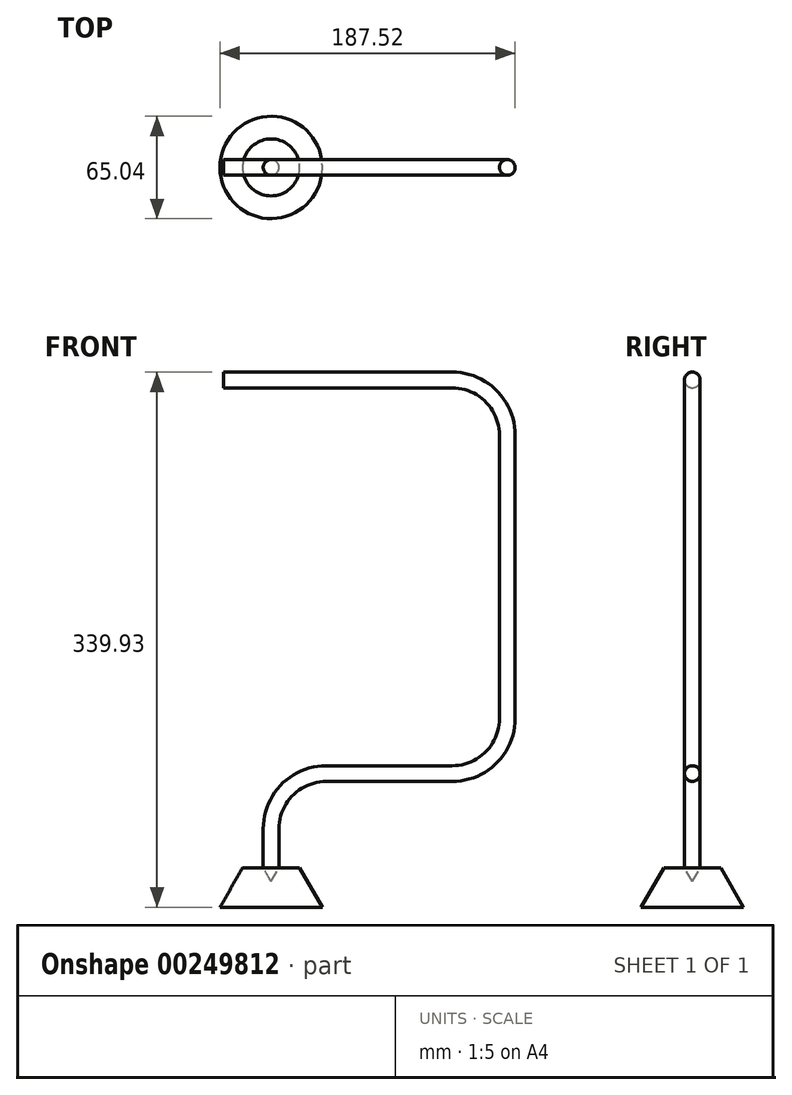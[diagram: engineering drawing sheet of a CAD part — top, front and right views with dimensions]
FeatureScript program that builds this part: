
annotation { "Feature Type Name" : "Feature", "Feature Type Description" : "" }
export const myFeature = defineFeature(function(context is Context, id is Id, definition is map)
    precondition{}
    {
        {
            var Q0;
            Q0=qCreatedBy(makeId("Front.planeOp"),FACE);
            var sketch = newSketch(context, id + "F0", { "sketchPlane" : qUnion([Q0])});
            skLineSegment(sketch, "E0", {"start": v(0, 0) * mm, "end": v(145.15, 0) * mm});
            skLineSegment(sketch, "E1", {"start": v(180.15, -35) * mm, "end": v(180.15, -215) * mm});
            skPoint(sketch, "E2.visualSharp", {"position": v(180.15, 0) * mm});
            skArc(sketch, "E2.filletArc", {"start": v(180.15, -35) * mm, "mid": v(169.9, -10.25) * mm, "end": v(145.15, 0) * mm});
            skLineSegment(sketch, "E3", {"start": v(145.15, -250) * mm, "end": v(65.15, -250) * mm});
            skLineSegment(sketch, "E4", {"start": v(30.15, -285) * mm, "end": v(30.15, -309.93) * mm});
            skPoint(sketch, "E5.visualSharp", {"position": v(180.15, -250) * mm});
            skArc(sketch, "E5.filletArc", {"start": v(145.15, -250) * mm, "mid": v(169.9, -239.75) * mm, "end": v(180.15, -215) * mm});
            skPoint(sketch, "E6.visualSharp", {"position": v(30.15, -250) * mm});
            skArc(sketch, "E6.filletArc", {"start": v(65.15, -250) * mm, "mid": v(40.4, -260.25) * mm, "end": v(30.15, -285) * mm});
            skSolve(sketch);
        }
        {
            var Q0;
            Q0=qCreatedBy(makeId("Right.planeOp"),FACE);
            var sketch = newSketch(context, id + "F1", { "sketchPlane" : qUnion([Q0])});
            skCircle(sketch, "E7", {"center": v(0, 0) * mm, "radius": 5 * mm});
            skSolve(sketch);
        }
        {
            var Q0;
            Q0=makeQuery(id+"F1.imprint","IMPRINT",FACE,{"disambiguationData":[TD([[makeQuery(id+"F1.imprint","IMPRINT",EDGE,{"derivedFrom":sQuery(id+"F1.wireOp",EDGE,"E7")}),1.0]])]});
            var Q1;
            Q1=sQuery(id+"F0.wireOp",EDGE,"E1");
            var Q2;
            Q2=sQuery(id+"F0.wireOp",EDGE,"E2.filletArc");
            var Q3;
            Q3=sQuery(id+"F0.wireOp",EDGE,"E0");
            var Q4;
            Q4=sQuery(id+"F0.wireOp",EDGE,"E5.filletArc");
            var Q5;
            Q5=sQuery(id+"F0.wireOp",EDGE,"E3");
            var Q6;
            Q6=sQuery(id+"F0.wireOp",EDGE,"E6.filletArc");
            var Q7;
            Q7=sQuery(id+"F0.wireOp",EDGE,"E4");
            sweep(context, id + "F2", {"profiles" : qUnion([Q0]), "path" : qUnion([Q1, Q2, Q3, Q4, Q5, Q6, Q7])});
        }
        {
            var Q0;
            Q0=makeQuery(id+"F2.opSweep","CAP_FACE",FACE,{"disambiguationData":[OSD([sQuery(id+"F0.wireOp",VERTEX,"E4.end"),sQuery(id+"F1.wireOp",EDGE,"E7")])],"isStart":false});
            var sketch = newSketch(context, id + "F3", { "sketchPlane" : qUnion([Q0])});
            skCircle(sketch, "E8.0", {"center": v(30.15, 0) * mm, "radius": 5 * mm});
            skCircle(sketch, "E9", {"center": v(30.15, 0) * mm, "radius": 18.09 * mm});
            skSolve(sketch);
        }
        {
            var Q0;
            Q0=makeQuery(id+"F3.imprint","IMPRINT",FACE,{"disambiguationData":[TD([[makeQuery(id+"F3.imprint","IMPRINT",EDGE,{"derivedFrom":sQuery(id+"F3.wireOp",EDGE,"E8.0")}),-1.0]])]});
            extrude(context, id + "F4", {"entities" : qUnion([Q0]), "depth" : 25 * mm, "hasDraft" : true, "draftAngle" : 30 * degree});
        }
    });
